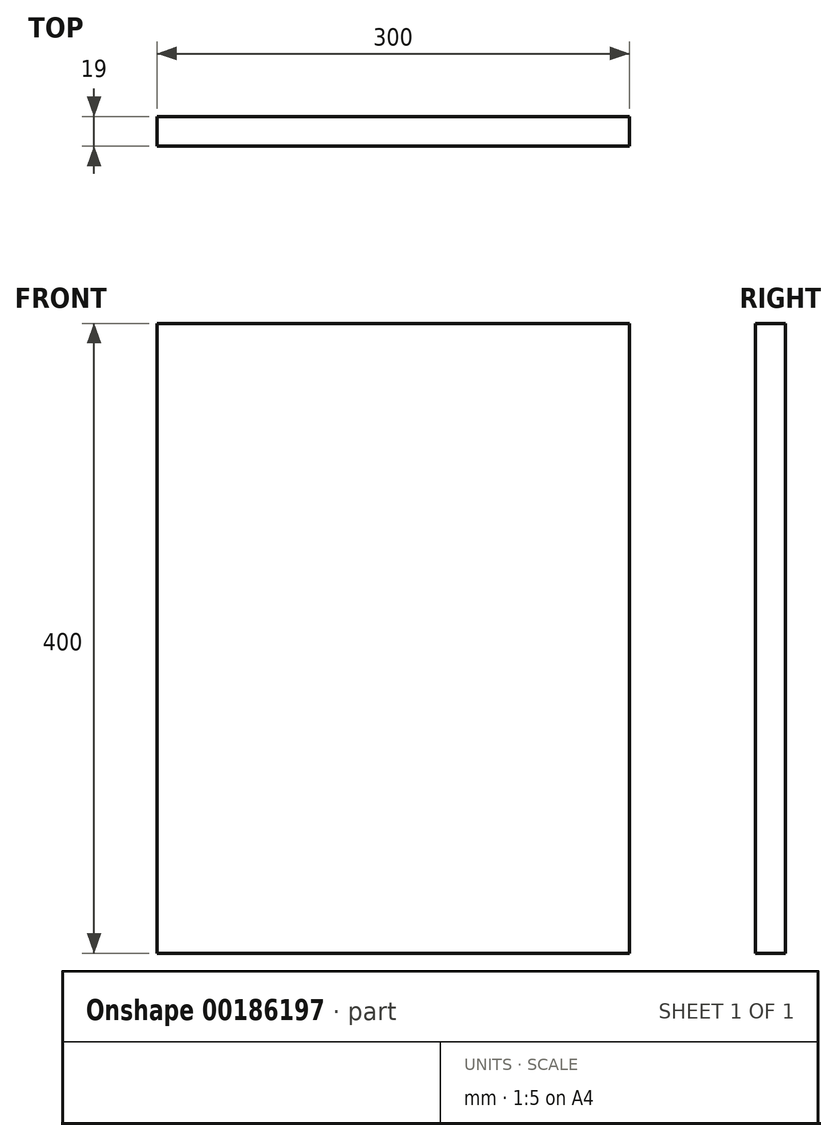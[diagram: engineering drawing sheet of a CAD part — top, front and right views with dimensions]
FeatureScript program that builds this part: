
annotation { "Feature Type Name" : "Feature", "Feature Type Description" : "" }
export const myFeature = defineFeature(function(context is Context, id is Id, definition is map)
    precondition{}
    {
        {
            var Q0;
            Q0=qCreatedBy(makeId("Front.planeOp"),FACE);
            var sketch = newSketch(context, id + "F0", { "sketchPlane" : qUnion([Q0])});
            skLineSegment(sketch, "E0.bottom", {"start": v(-137.17, 207.19) * mm, "end": v(162.83, 207.19) * mm});
            skLineSegment(sketch, "E0.top", {"start": v(-137.17, -192.81) * mm, "end": v(162.83, -192.81) * mm});
            skLineSegment(sketch, "E0.left", {"start": v(-137.17, 207.19) * mm, "end": v(-137.17, -192.81) * mm});
            skLineSegment(sketch, "E0.right", {"start": v(162.83, 207.19) * mm, "end": v(162.83, -192.81) * mm});
            skSolve(sketch);
        }
        {
            var Q0;
            Q0 = qSketchRegion(id + "F0", true);
            extrude(context, id + "F1", {"entities" : qUnion([Q0]), "depth" : 19 * mm});
        }
    });
